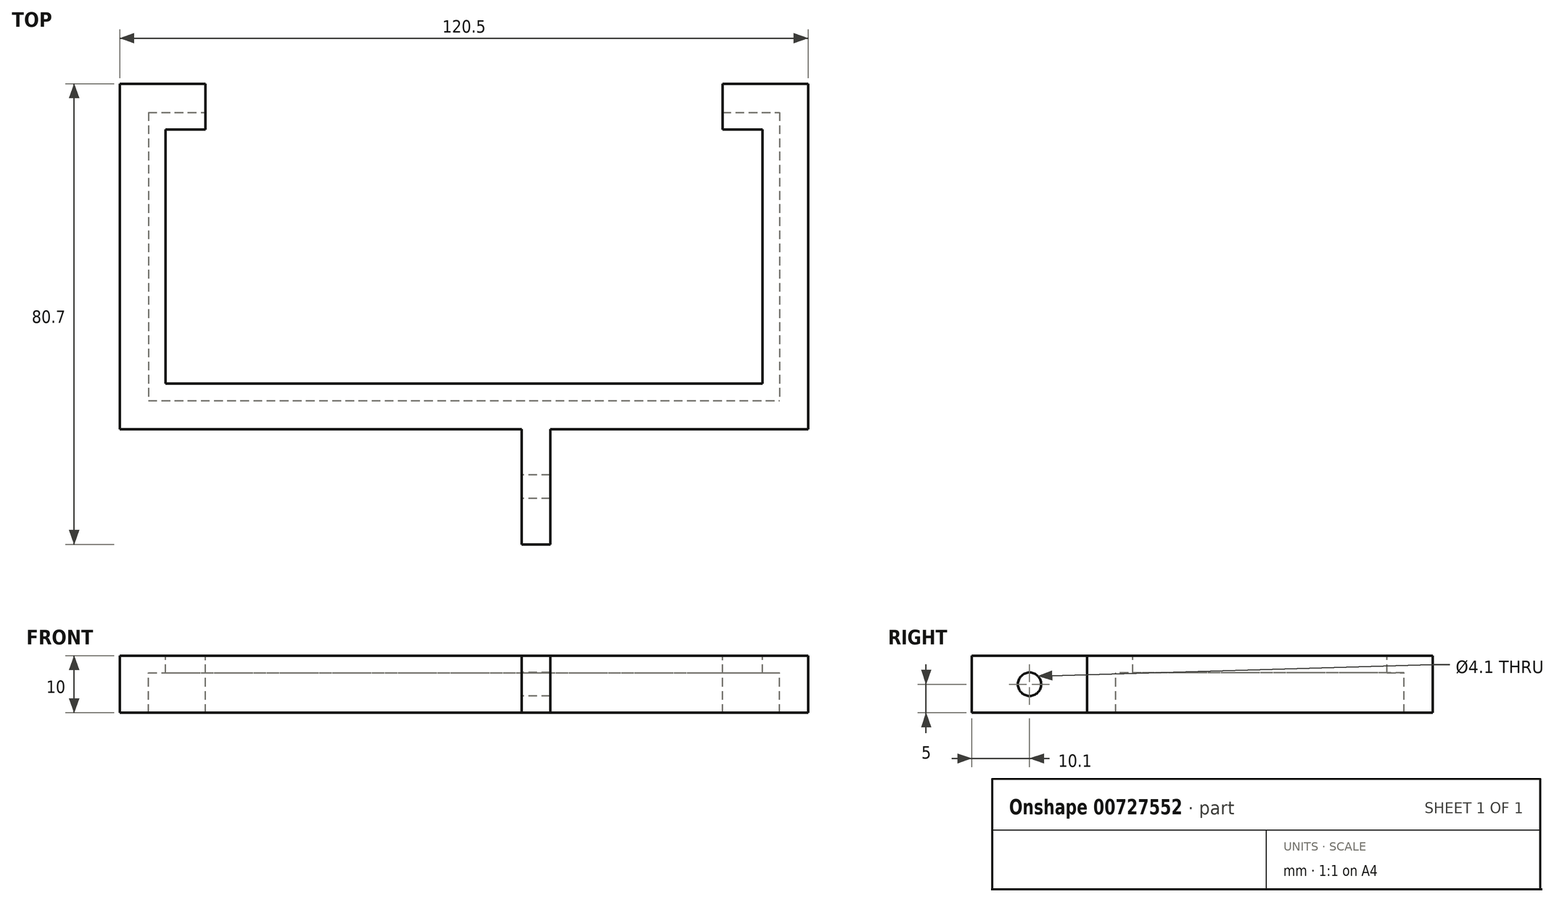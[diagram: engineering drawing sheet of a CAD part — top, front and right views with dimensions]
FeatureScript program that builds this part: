
annotation { "Feature Type Name" : "Feature", "Feature Type Description" : "" }
export const myFeature = defineFeature(function(context is Context, id is Id, definition is map)
    precondition{}
    {
        {
            var Q0;
            Q0=qCreatedBy(makeId("Top.planeOp"),FACE);
            var sketch = newSketch(context, id + "F0", { "sketchPlane" : qUnion([Q0])});
            skLineSegment(sketch, "E0.bottom", {"start": v(-58.2, 0.1) * mm, "end": v(52.3, 0.1) * mm});
            skLineSegment(sketch, "E0.top", {"start": v(-58.2, -50.4) * mm, "end": v(52.3, -50.4) * mm});
            skLineSegment(sketch, "E0.left", {"start": v(-58.2, 0.1) * mm, "end": v(-58.2, -50.4) * mm});
            skLineSegment(sketch, "E0.right", {"start": v(52.3, 0.1) * mm, "end": v(52.3, -50.4) * mm});
            skLineSegment(sketch, "E1.bottom", {"start": v(-63.2, 5.1) * mm, "end": v(57.3, 5.1) * mm});
            skLineSegment(sketch, "E1.top", {"start": v(-63.2, -55.4) * mm, "end": v(57.3, -55.4) * mm});
            skLineSegment(sketch, "E1.left", {"start": v(-63.2, 5.1) * mm, "end": v(-63.2, -55.4) * mm});
            skLineSegment(sketch, "E1.right", {"start": v(57.3, 5.1) * mm, "end": v(57.3, -55.4) * mm});
            skLineSegment(sketch, "E2", {"start": v(-48.2, -2.9) * mm, "end": v(-48.2, 5.1) * mm});
            skLineSegment(sketch, "E3", {"start": v(42.3, -2.9) * mm, "end": v(42.3, 5.1) * mm});
            skPoint(sketch, "E4", {"position": v(-2.95, -55.4) * mm});
            skLineSegment(sketch, "E5.bottom", {"start": v(7.15, -55.4) * mm, "end": v(12.15, -55.4) * mm});
            skLineSegment(sketch, "E5.top", {"start": v(7.15, -75.6) * mm, "end": v(12.15, -75.6) * mm});
            skLineSegment(sketch, "E5.left", {"start": v(7.15, -55.4) * mm, "end": v(7.15, -75.6) * mm});
            skLineSegment(sketch, "E5.right", {"start": v(12.15, -55.4) * mm, "end": v(12.15, -75.6) * mm});
            skLineSegment(sketch, "E6", {"start": v(-58.2, -40.4) * mm, "end": v(52.3, -40.4) * mm});
            skLineSegment(sketch, "E7.bottom", {"start": v(-55.2, -2.9) * mm, "end": v(49.3, -2.9) * mm});
            skLineSegment(sketch, "E7.top", {"start": v(-55.2, -47.4) * mm, "end": v(49.3, -47.4) * mm});
            skLineSegment(sketch, "E7.left", {"start": v(-55.2, -2.9) * mm, "end": v(-55.2, -47.4) * mm});
            skLineSegment(sketch, "E7.right", {"start": v(49.3, -2.9) * mm, "end": v(49.3, -47.4) * mm});
            skSolve(sketch);
        }
        {
            var Q0;
            {var subQ10=sQuery(id+"F0.wireOp",EDGE,"E0.top");Q0=makeQuery(id+"F0.imprint","IMPRINT",FACE,{"disambiguationData":[TD([[makeQuery(id+"F0.imprint","IMPRINT",EDGE,{"derivedFrom":subQ10}),-1.0]])]});}
            var Q1;
            Q1=makeQuery(id+"F0.imprint","IMPRINT",FACE,{"disambiguationData":[TD([[makeQuery(id+"F0.imprint","IMPRINT",EDGE,{"derivedFrom":sQuery(id+"F0.wireOp",EDGE,"E5.top")}),1.0]])]});
            extrude(context, id + "F1", {"entities" : qUnion([Q0, Q1]), "oppositeDirection" : true, "depth" : 10 * mm, "offsetDistance" : 25 * mm});
        }
        {
            var Q0;
            Q0=makeQuery(id+"F1.opExtrude","SWEPT_FACE",FACE,{"disambiguationData":[OSD([sQuery(id+"F0.wireOp",EDGE,"E5.right")])]});
            var sketch = newSketch(context, id + "F2", { "sketchPlane" : qUnion([Q0])});
            skLineSegment(sketch, "E8", {"start": v(-75.6, -10) * mm, "end": v(-55.4, 0) * mm, "construction": true});
            skPoint(sketch, "E9", {"position": v(-65.5, -5) * mm});
            skSolve(sketch);
        }
        {
            var Q0;
            Q0=sQuery(id+"F2.wireOp",VERTEX,"E9");
            var Q1;
            Q1=makeQuery(id+"F1.opExtrude","SWEPT_BODY",BODY,{"disambiguationData":[OSD([sQuery(id+"F0.wireOp",EDGE,"E0.bottom"),sQuery(id+"F0.wireOp",EDGE,"E0.top"),sQuery(id+"F0.wireOp",EDGE,"E0.left"),sQuery(id+"F0.wireOp",EDGE,"E0.right"),sQuery(id+"F0.wireOp",EDGE,"E1.bottom"),sQuery(id+"F0.wireOp",EDGE,"E1.top"),sQuery(id+"F0.wireOp",EDGE,"E1.left"),sQuery(id+"F0.wireOp",EDGE,"E1.right"),sQuery(id+"F0.wireOp",EDGE,"E2"),sQuery(id+"F0.wireOp",EDGE,"E3"),sQuery(id+"F0.wireOp",EDGE,"E5.top"),sQuery(id+"F0.wireOp",EDGE,"E5.left"),sQuery(id+"F0.wireOp",EDGE,"E5.right")])]});
            hole(context, id + "F3", {"style" : HoleStyle.SIMPLE, "endStyle" : HoleEndStyle.BLIND, "holeDiameter" : 4.1 * mm, "majorDiameter" : 5 * mm, "holeDepth" : 7 * mm, "tappedDepth" : 30 * mm, "tapClearance" : 3, "startFromSketch" : true, "locations" : qUnion([Q0]), "scope" : qUnion([Q1])});
        }
        {
            var Q0;
            {var subQ5=sQuery(id+"F0.wireOp",EDGE,"E0.top");Q0=makeQuery(id+"F0.imprint","IMPRINT",FACE,{"disambiguationData":[TD([[makeQuery(id+"F0.imprint","IMPRINT",EDGE,{"derivedFrom":subQ5}),1.0]])]});}
            var Q1;
            {var subQ5=sQuery(id+"F0.wireOp",EDGE,"E2");var subQ6=sQuery(id+"F0.wireOp",EDGE,"E0.bottom");var subQ7=makeQuery(id+"F0.imprint","INTERSECT",VERTEX,{"derivedFrom":[subQ6,subQ5]});Q1=makeQuery(id+"F0.imprint","IMPRINT",FACE,{"disambiguationData":[TD([[makeQuery(id+"F0.imprint","IMPRINT",EDGE,{"disambiguationData":[TD([[subQ7,1.0]])],"derivedFrom":subQ6}),-1.0]])]});}
            var Q2;
            {var subQ1=sQuery(id+"F0.wireOp",EDGE,"E0.right");var subQ5=sQuery(id+"F0.wireOp",EDGE,"E0.bottom");var subQ6=makeQuery(id+"F0.imprint","INTERSECT",VERTEX,{"derivedFrom":[subQ5,subQ1]});Q2=makeQuery(id+"F0.imprint","IMPRINT",FACE,{"disambiguationData":[TD([[makeQuery(id+"F0.imprint","IMPRINT",EDGE,{"disambiguationData":[TD([[subQ6,1.0]])],"derivedFrom":subQ5}),-1.0]])]});}
            extrude(context, id + "F4", {"entities" : qUnion([Q0, Q1, Q2]), "operationType" : NewBodyOperationType.ADD, "oppositeDirection" : true, "depth" : 3 * mm, "offsetDistance" : 25 * mm});
        }
    });
